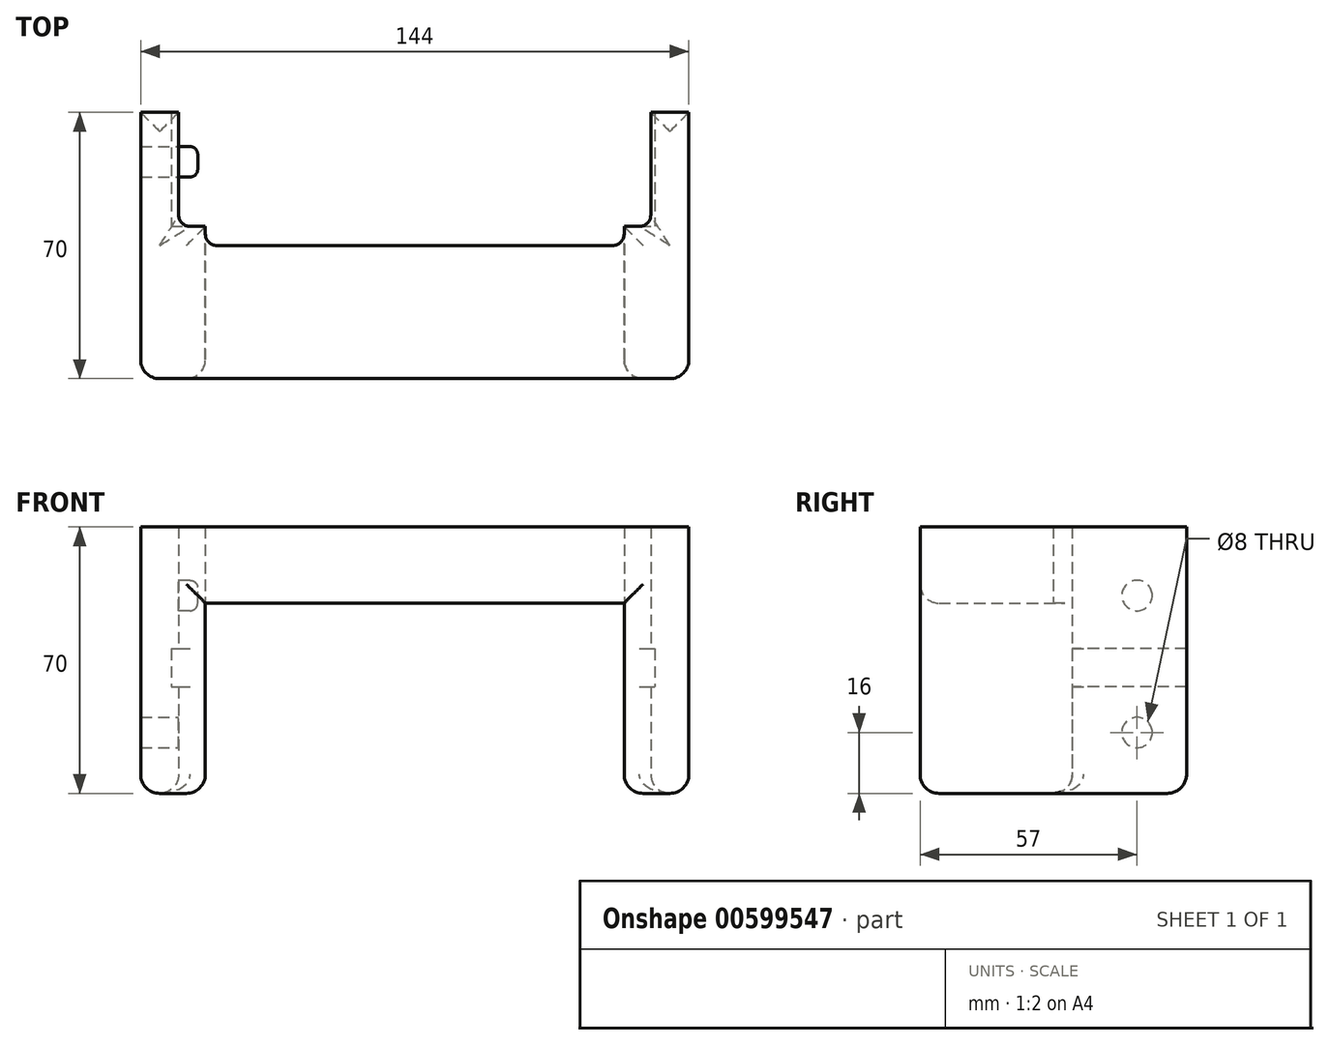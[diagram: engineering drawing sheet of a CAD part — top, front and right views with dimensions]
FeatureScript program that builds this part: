
annotation { "Feature Type Name" : "Feature", "Feature Type Description" : "" }
export const myFeature = defineFeature(function(context is Context, id is Id, definition is map)
    precondition{}
    {
        {
            var Q0;
            Q0=qCreatedBy(makeId("Top.planeOp"),FACE);
            var sketch = newSketch(context, id + "F0", { "sketchPlane" : qUnion([Q0])});
            skLineSegment(sketch, "E0.bottom", {"start": v(-72, 30) * mm, "end": v(-62, 30) * mm});
            skLineSegment(sketch, "E0.top", {"start": v(-72, -40) * mm, "end": v(72, -40) * mm});
            skLineSegment(sketch, "E0.left", {"start": v(-72, 30) * mm, "end": v(-72, -40) * mm});
            skLineSegment(sketch, "E0.right", {"start": v(72, 30) * mm, "end": v(72, -40) * mm});
            skLineSegment(sketch, "E1.top", {"start": v(-62, 0) * mm, "end": v(62, 0) * mm});
            skLineSegment(sketch, "E1.left", {"start": v(-62, 30) * mm, "end": v(-62, 0) * mm});
            skLineSegment(sketch, "E1.right", {"start": v(62, 30) * mm, "end": v(62, 0) * mm});
            skLineSegment(sketch, "E2.trimOffspring", {"start": v(62, 30) * mm, "end": v(72, 30) * mm});
            skLineSegment(sketch, "E3.bottom", {"start": v(-55, 0) * mm, "end": v(55, 0) * mm});
            skLineSegment(sketch, "E3.top", {"start": v(-55, -5) * mm, "end": v(55, -5) * mm});
            skLineSegment(sketch, "E3.left", {"start": v(-55, 0) * mm, "end": v(-55, -5) * mm});
            skLineSegment(sketch, "E3.right", {"start": v(55, 0) * mm, "end": v(55, -5) * mm});
            skSolve(sketch);
        }
        {
            var Q0;
            Q0=makeQuery(id+"F0.imprint","IMPRINT",FACE,{"disambiguationData":[TD([[makeQuery(id+"F0.imprint","IMPRINT",EDGE,{"derivedFrom":sQuery(id+"F0.wireOp",EDGE,"E0.bottom")}),-1.0]])]});
            extrude(context, id + "F1", {"entities" : qUnion([Q0]), "depth" : 70 * mm, "offsetDistance" : 25 * mm});
        }
        {
            var Q0;
            Q0=makeQuery(id+"F1.opExtrude","SWEPT_FACE",FACE,{"disambiguationData":[OSD([sQuery(id+"F0.wireOp",EDGE,"E1.left")])]});
            var sketch = newSketch(context, id + "F2", { "sketchPlane" : qUnion([Q0])});
            skCircle(sketch, "E4", {"center": v(17, 16) * mm, "radius": 4 * mm});
            skLineSegment(sketch, "E5.bottom", {"start": v(30, 38) * mm, "end": v(0, 38) * mm});
            skLineSegment(sketch, "E5.top", {"start": v(30, 28) * mm, "end": v(0, 28) * mm});
            skLineSegment(sketch, "E5.left", {"start": v(30, 38) * mm, "end": v(30, 28) * mm});
            skLineSegment(sketch, "E5.right", {"start": v(0, 38) * mm, "end": v(0, 28) * mm});
            skCircle(sketch, "E6", {"center": v(17, 52) * mm, "radius": 4 * mm});
            skSolve(sketch);
        }
        {
            var Q0;
            Q0=makeQuery(id+"F2.imprint","IMPRINT",FACE,{"disambiguationData":[TD([[makeQuery(id+"F2.imprint","IMPRINT",EDGE,{"derivedFrom":sQuery(id+"F2.wireOp",EDGE,"E5.bottom")}),1.0]])]});
            extrude(context, id + "F3", {"entities" : qUnion([Q0]), "operationType" : NewBodyOperationType.REMOVE, "oppositeDirection" : true, "depth" : 2 * mm, "offsetDistance" : 25 * mm, "hasSecondDirection" : true, "secondDirectionOppositeDirection" : false, "secondDirectionDepth" : 125 * mm});
        }
        {
            var Q0;
            Q0=makeQuery(id+"F2.imprint","IMPRINT",FACE,{"disambiguationData":[TD([[makeQuery(id+"F2.imprint","IMPRINT",EDGE,{"derivedFrom":sQuery(id+"F2.wireOp",EDGE,"E4")}),1.0]])]});
            extrude(context, id + "F4", {"entities" : qUnion([Q0]), "operationType" : NewBodyOperationType.REMOVE, "oppositeDirection" : true, "depth" : 25 * mm, "offsetDistance" : 25 * mm});
        }
        {
            var Q0;
            Q0=makeQuery(id+"F2.imprint","IMPRINT",FACE,{"disambiguationData":[TD([[makeQuery(id+"F2.imprint","IMPRINT",EDGE,{"derivedFrom":sQuery(id+"F2.wireOp",EDGE,"E6")}),1.0]])]});
            extrude(context, id + "F5", {"entities" : qUnion([Q0]), "operationType" : NewBodyOperationType.ADD, "depth" : 5 * mm, "offsetDistance" : 25 * mm});
        }
        {
            var Q0;
            Q0=makeQuery(id+"F1.opExtrude","SWEPT_FACE",FACE,{"disambiguationData":[OSD([sQuery(id+"F0.wireOp",EDGE,"E3.top")])]});
            var sketch = newSketch(context, id + "F6", { "sketchPlane" : qUnion([Q0])});
            skLineSegment(sketch, "E7.bottom", {"start": v(55, 0) * mm, "end": v(-55, 0) * mm});
            skLineSegment(sketch, "E7.top", {"start": v(55, 50) * mm, "end": v(-55, 50) * mm});
            skLineSegment(sketch, "E7.left", {"start": v(55, 0) * mm, "end": v(55, 50) * mm});
            skLineSegment(sketch, "E7.right", {"start": v(-55, 0) * mm, "end": v(-55, 50) * mm});
            skSolve(sketch);
        }
        {
            var Q0;
            Q0=makeQuery(id+"F6.imprint","IMPRINT",FACE,{"disambiguationData":[TD([[makeQuery(id+"F6.imprint","IMPRINT",EDGE,{"derivedFrom":sQuery(id+"F6.wireOp",EDGE,"E7.bottom")}),-1.0]])]});
            extrude(context, id + "F7", {"entities" : qUnion([Q0]), "operationType" : NewBodyOperationType.REMOVE, "oppositeDirection" : true, "depth" : 100 * mm, "offsetDistance" : 25 * mm});
        }
        {
            var Q0;
            Q0=makeQuery(id+"F1.opExtrude","SWEPT_EDGE",EDGE,{"disambiguationData":[OSD([sQuery(id+"F0.wireOp",EDGE,"E0.top"),sQuery(id+"F0.wireOp",EDGE,"E0.left")])]});
            var Q1;
            Q1=makeQuery(id+"F1.opExtrude","SWEPT_EDGE",EDGE,{"disambiguationData":[OSD([sQuery(id+"F0.wireOp",EDGE,"E0.top"),sQuery(id+"F0.wireOp",EDGE,"E0.right")])]});
            var Q2;
            Q2=makeQuery(id+"F7.boolean.opBoolean","INTERSECT",EDGE,{"derivedFrom":[makeQuery(id+"F1.opExtrude","SWEPT_FACE",FACE,{"disambiguationData":[OSD([sQuery(id+"F0.wireOp",EDGE,"E0.top")])]}),makeQuery(id+"F7.opExtrude","SWEPT_FACE",FACE,{"disambiguationData":[OSD([sQuery(id+"F6.wireOp",EDGE,"E7.right")])]})]});
            var Q3;
            Q3=makeQuery(id+"F7.boolean.opBoolean","INTERSECT",EDGE,{"derivedFrom":[makeQuery(id+"F1.opExtrude","SWEPT_FACE",FACE,{"disambiguationData":[OSD([sQuery(id+"F0.wireOp",EDGE,"E0.top")])]}),makeQuery(id+"F7.opExtrude","SWEPT_FACE",FACE,{"disambiguationData":[OSD([sQuery(id+"F6.wireOp",EDGE,"E7.left")])]})]});
            var Q4;
            Q4=makeQuery(id+"F7.boolean.opBoolean","INTERSECT",EDGE,{"derivedFrom":[makeQuery(id+"F1.opExtrude","SWEPT_FACE",FACE,{"disambiguationData":[OSD([sQuery(id+"F0.wireOp",EDGE,"E0.top")])]}),makeQuery(id+"F7.opExtrude","SWEPT_FACE",FACE,{"disambiguationData":[OSD([sQuery(id+"F6.wireOp",EDGE,"E7.top")])]})]});
            var Q5;
            {var subQ0=sQuery(id+"F0.wireOp",EDGE,"E1.left");var subQ1=sQuery(id+"F0.wireOp",EDGE,"E1.top");var subQ2=sQuery(id+"F0.wireOp",EDGE,"E3.left");var subQ3=sQuery(id+"F0.wireOp",EDGE,"E0.left");var subQ4=sQuery(id+"F0.wireOp",EDGE,"E0.top");var subQ5=sQuery(id+"F0.wireOp",EDGE,"E0.bottom");Q5=makeQuery(id+"F7.boolean.opBoolean","SPLIT",FACE,{"disambiguationData":[TD([makeQuery(id+"F1.opExtrude","SWEPT_FACE",FACE,{"disambiguationData":[OSD([subQ5])]})])],"derivedFrom":makeQuery(id+"F1.opExtrude","CAP_FACE",FACE,{"disambiguationData":[OSD([subQ5,subQ4,subQ3,sQuery(id+"F0.wireOp",EDGE,"E0.right"),subQ1,subQ0,sQuery(id+"F0.wireOp",EDGE,"E1.right"),sQuery(id+"F0.wireOp",EDGE,"E2.trimOffspring"),sQuery(id+"F0.wireOp",EDGE,"E3.top"),subQ2,sQuery(id+"F0.wireOp",EDGE,"E3.right")])],"isStart":true})});}
            var Q6;
            {var subQ0=sQuery(id+"F0.wireOp",EDGE,"E1.right");var subQ1=sQuery(id+"F0.wireOp",EDGE,"E1.top");var subQ2=sQuery(id+"F0.wireOp",EDGE,"E3.right");var subQ3=sQuery(id+"F0.wireOp",EDGE,"E0.right");var subQ4=sQuery(id+"F0.wireOp",EDGE,"E0.top");var subQ5=sQuery(id+"F0.wireOp",EDGE,"E2.trimOffspring");Q6=makeQuery(id+"F7.boolean.opBoolean","SPLIT",FACE,{"disambiguationData":[TD([makeQuery(id+"F1.opExtrude","SWEPT_FACE",FACE,{"disambiguationData":[OSD([subQ3])]})])],"derivedFrom":makeQuery(id+"F1.opExtrude","CAP_FACE",FACE,{"disambiguationData":[OSD([sQuery(id+"F0.wireOp",EDGE,"E0.bottom"),subQ4,sQuery(id+"F0.wireOp",EDGE,"E0.left"),subQ3,subQ1,sQuery(id+"F0.wireOp",EDGE,"E1.left"),subQ0,subQ5,sQuery(id+"F0.wireOp",EDGE,"E3.top"),sQuery(id+"F0.wireOp",EDGE,"E3.left"),subQ2])],"isStart":true})});}
            fillet(context, id + "F8", {"entities" : qUnion([Q0, Q1, Q2, Q3, Q4, Q5, Q6]), "radius" : 5 * mm, "tangentPropagation" : true, "allowEdgeOverflow" : false});
        }
        {
            var Q0;
            Q0=makeQuery(id+"F5.opExtrude","CAP_EDGE",EDGE,{"disambiguationData":[OSD([sQuery(id+"F2.wireOp",EDGE,"E6")])],"isStart":false});
            fillet(context, id + "F9", {"entities" : qUnion([Q0]), "radius" : 2 * mm, "tangentPropagation" : true, "allowEdgeOverflow" : false});
        }
        {
            var Q0;
            {var subQ0=sQuery(id+"F0.wireOp",EDGE,"E1.left");var subQ1=sQuery(id+"F0.wireOp",EDGE,"E1.top");Q0=makeQuery(id+"F3.boolean.opBoolean","SPLIT",EDGE,{"disambiguationData":[TD([makeQuery(id+"F3.opExtrude","SWEPT_FACE",FACE,{"disambiguationData":[OSD([sQuery(id+"F2.wireOp",EDGE,"E5.bottom")])]})])],"derivedFrom":makeQuery(id+"F1.opExtrude","SWEPT_EDGE",EDGE,{"disambiguationData":[OSD([subQ1,subQ0])]})});}
            var Q1;
            {var subQ0=sQuery(id+"F0.wireOp",EDGE,"E1.left");var subQ1=sQuery(id+"F0.wireOp",EDGE,"E1.top");Q1=makeQuery(id+"F3.boolean.opBoolean","SPLIT",EDGE,{"disambiguationData":[TD([makeQuery(id+"F3.opExtrude","SWEPT_FACE",FACE,{"disambiguationData":[OSD([sQuery(id+"F2.wireOp",EDGE,"E5.top")])]})])],"derivedFrom":makeQuery(id+"F1.opExtrude","SWEPT_EDGE",EDGE,{"disambiguationData":[OSD([subQ1,subQ0])]})});}
            var Q2;
            Q2=makeQuery(id+"F1.opExtrude","SWEPT_EDGE",EDGE,{"disambiguationData":[OSD([sQuery(id+"F0.wireOp",EDGE,"E1.top"),sQuery(id+"F0.wireOp",EDGE,"E1.right")])]});
            var Q3;
            Q3=makeQuery(id+"F1.opExtrude","SWEPT_EDGE",EDGE,{"disambiguationData":[OSD([sQuery(id+"F0.wireOp",EDGE,"E3.top"),sQuery(id+"F0.wireOp",EDGE,"E3.right")])]});
            var Q4;
            Q4=makeQuery(id+"F1.opExtrude","SWEPT_EDGE",EDGE,{"disambiguationData":[OSD([sQuery(id+"F0.wireOp",EDGE,"E3.top"),sQuery(id+"F0.wireOp",EDGE,"E3.left")])]});
            fillet(context, id + "F10", {"entities" : qUnion([Q0, Q1, Q2, Q3, Q4]), "radius" : 3 * mm, "tangentPropagation" : true, "allowEdgeOverflow" : false});
        }
    });
